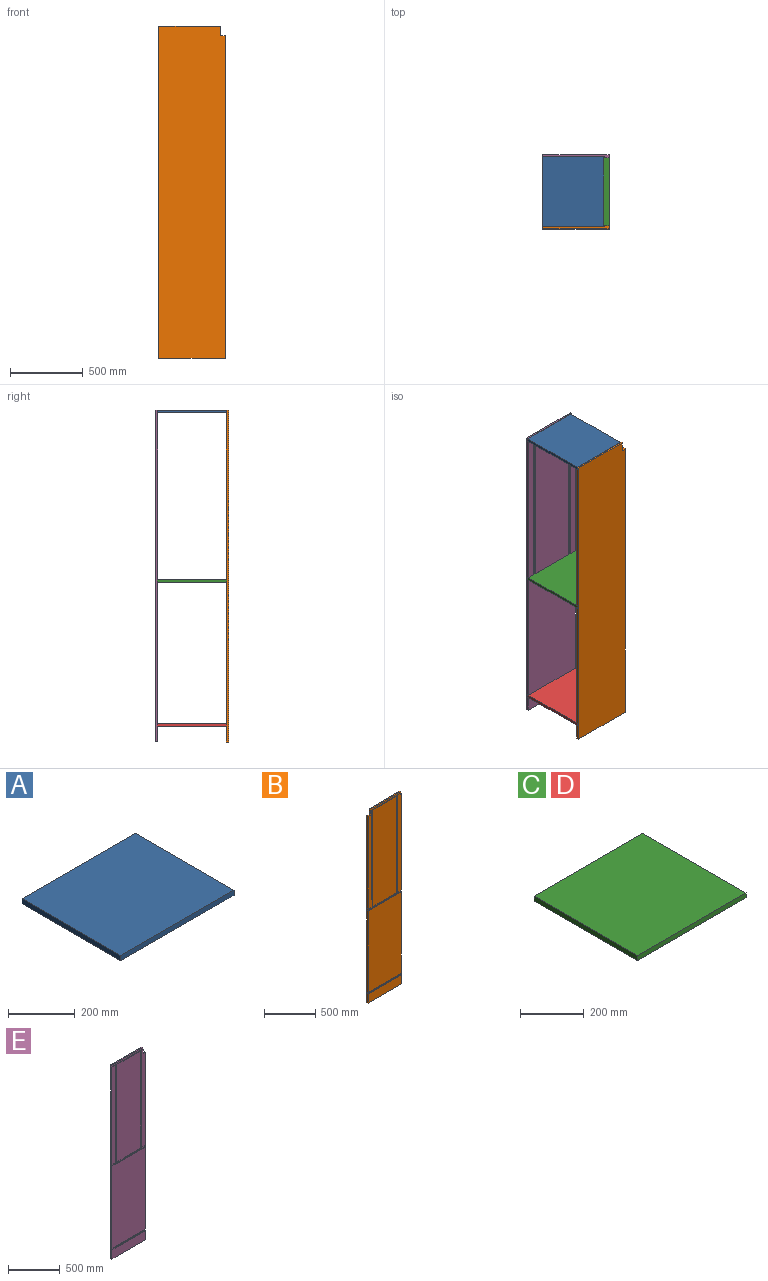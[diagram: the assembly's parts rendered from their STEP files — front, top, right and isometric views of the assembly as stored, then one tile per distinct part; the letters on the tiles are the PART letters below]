
ASSEMBLY  parts=5 mates=12
PART A: 6 faces, bbox 481.3x419.1x19.1 mm
  f0: plane 419.1x19.05mm, normal (-1,0,0), area 7983.9mm2, adj f1,f3,f4,f5
  f1: plane 481.33x19.05mm, normal (0,-1,0), area 9169.3mm2, adj f0,f2,f4,f5
  f2: plane 419.1x19.05mm, normal (1,0,0), area 7983.9mm2, adj f1,f3,f4,f5
  f3: plane 481.33x19.05mm, normal (0,1,0), area 9169.3mm2, adj f0,f2,f4,f5
  f4: plane 481.33x419.1mm, normal (0,0,1), area 201725.4mm2, adj f0,f1,f2,f3
  f5: plane 481.33x419.1mm, normal (0,0,-1), area 201725.4mm2, adj f0,f1,f2,f3
PART B: 26 faces, bbox 457.2x19.1x2286 mm
  f0: plane 1149.1x50.8mm, normal (0,-1,0), area 56878.3mm2, adj f2,f3,f9,f12,f13,f23
  f1: plane 1149.1x323.85mm, normal (0,-1,0), area 372134.7mm2, adj f2,f3,f21,f24
  f2: plane 425.2x6.35mm, normal (0,0,1), area 2548.8mm2, adj f0,f1,f6,f11,f13,f14,f20,f21
  f3: plane 457.2x6.35mm, normal (0,0,-1), area 2752mm2, adj f0,f1,f6,f9,f11,f16,f20,f21
  f4: plane 425.2x12.7mm, normal (0,0,1), area 5400mm2, adj f8,f11,f13,f14
  f5: plane 971.3x457.2mm, normal (0,-1,0), area 444076.5mm2, adj f9,f11,f15,f18
  f6: plane 1149.1x50.8mm, normal (0,-1,0), area 58374.1mm2, adj f2,f3,f11,f20
  f7: plane 457.2x107.7mm, normal (0,-1,0), area 49238.6mm2, adj f9,f10,f11,f17
  f8: plane 2286x457.2mm, normal (0,1,0), area 1043045.7mm2, adj f4,f9,f10,f11,f12,f13
  f9: plane 2219.96x19.05mm, normal (-1,0,0), area 42045.1mm2, adj f0,f3,f5,f7,f8,f10,f12,f15
  f10: plane 457.2x19.05mm, normal (0,0,-1), area 8709.7mm2, adj f7,f8,f9,f11
  f11: plane 2286x19.05mm, normal (1,0,0), area 43180.6mm2, adj f2,f3,f4,f5,f6,f7,f8,f10
  f12: plane 32x19.05mm, normal (0,0,1), area 609.7mm2, adj f0,f8,f9,f13
  f13: plane 66.04x19.05mm, normal (-1,0,0), area 1135.5mm2, adj f0,f2,f4,f8,f12,f14
  f14: plane 425.2x19.3mm, normal (0,-1,0), area 8208mm2, adj f2,f4,f11,f13
  f15: plane 457.2x6.35mm, normal (0,0,1), area 2903.2mm2, adj f5,f9,f11,f16
  f16: plane 457.2x19.3mm, normal (0,-1,0), area 8825.8mm2, adj f3,f9,f11,f15
  f17: plane 457.2x6.35mm, normal (0,0,1), area 2903.2mm2, adj f7,f9,f11,f19
  f18: plane 457.2x6.35mm, normal (0,0,-1), area 2903.2mm2, adj f5,f9,f11,f19
  f19: plane 457.2x19.3mm, normal (0,-1,0), area 8825.8mm2, adj f9,f11,f17,f18
  f20: plane 1149.1x4.76mm, normal (-1,0,0), area 5472.6mm2, adj f2,f3,f6,f22
  f21: plane 1149.1x4.76mm, normal (1,0,0), area 5472.6mm2, adj f1,f2,f3,f22
  f22: plane 1149.1x15.88mm, normal (0,-1,0), area 18241.9mm2, adj f2,f3,f20,f21
  f23: plane 1149.1x4.76mm, normal (1,0,0), area 5472.6mm2, adj f0,f2,f3,f25
  f24: plane 1149.1x4.76mm, normal (-1,0,0), area 5472.6mm2, adj f1,f2,f3,f25
  f25: plane 1149.1x15.88mm, normal (0,-1,0), area 18241.9mm2, adj f2,f3,f23,f24
PART C: 6 faces, bbox 481.3x457.2x19.1 mm
  f0: plane 457.2x19.05mm, normal (-1,0,0), area 8709.7mm2, adj f1,f3,f4,f5
  f1: plane 481.33x19.05mm, normal (0,-1,0), area 9169.3mm2, adj f0,f2,f4,f5
  f2: plane 457.2x19.05mm, normal (1,0,0), area 8709.7mm2, adj f1,f3,f4,f5
  f3: plane 481.33x19.05mm, normal (0,1,0), area 9169.3mm2, adj f0,f2,f4,f5
  f4: plane 481.33x457.2mm, normal (0,0,1), area 220064.1mm2, adj f0,f1,f2,f3
  f5: plane 481.33x457.2mm, normal (0,0,-1), area 220064.1mm2, adj f0,f1,f2,f3
PART D: same geometry as C
PART E: 26 faces, bbox 457.2x19.1x2286 mm
  f0: plane 1149.1x50.8mm, normal (0,-1,0), area 58374.1mm2, adj f2,f3,f7,f23
  f1: plane 1149.1x323.85mm, normal (0,-1,0), area 372134.7mm2, adj f2,f3,f21,f24
  f2: plane 425.2x6.35mm, normal (0,0,1), area 2548.8mm2, adj f0,f1,f6,f7,f12,f14,f20,f21
  f3: plane 457.2x6.35mm, normal (0,0,-1), area 2752mm2, adj f0,f1,f6,f7,f9,f16,f20,f21
  f4: plane 425.2x12.7mm, normal (0,0,1), area 5400mm2, adj f7,f11,f12,f14
  f5: plane 971.3x457.2mm, normal (0,-1,0), area 444076.5mm2, adj f7,f9,f15,f18
  f6: plane 1149.1x50.8mm, normal (0,-1,0), area 56878.3mm2, adj f2,f3,f9,f12,f13,f20
  f7: plane 2286x19.05mm, normal (-1,0,0), area 43180.6mm2, adj f0,f2,f3,f4,f5,f8,f10,f11
  f8: plane 457.2x19.05mm, normal (0,0,-1), area 8709.7mm2, adj f7,f9,f10,f11
  f9: plane 2219.96x19.05mm, normal (1,0,0), area 42045.1mm2, adj f3,f5,f6,f8,f10,f11,f13,f15
  f10: plane 457.2x107.7mm, normal (0,-1,0), area 49238.6mm2, adj f7,f8,f9,f17
  f11: plane 2286x457.2mm, normal (0,1,0), area 1043045.7mm2, adj f4,f7,f8,f9,f12,f13
  f12: plane 66.04x19.05mm, normal (1,0,0), area 1135.5mm2, adj f2,f4,f6,f11,f13,f14
  f13: plane 32x19.05mm, normal (0,0,1), area 609.7mm2, adj f6,f9,f11,f12
  f14: plane 425.2x19.3mm, normal (0,-1,0), area 8208mm2, adj f2,f4,f7,f12
  f15: plane 457.2x6.35mm, normal (0,0,1), area 2903.2mm2, adj f5,f7,f9,f16
  f16: plane 457.2x19.3mm, normal (0,-1,0), area 8825.8mm2, adj f3,f7,f9,f15
  f17: plane 457.2x6.35mm, normal (0,0,1), area 2903.2mm2, adj f7,f9,f10,f19
  f18: plane 457.2x6.35mm, normal (0,0,-1), area 2903.2mm2, adj f5,f7,f9,f19
  f19: plane 457.2x19.3mm, normal (0,-1,0), area 8825.8mm2, adj f7,f9,f17,f18
  f20: plane 1149.1x4.76mm, normal (-1,0,0), area 5472.6mm2, adj f2,f3,f6,f22
  f21: plane 1149.1x4.76mm, normal (1,0,0), area 5472.6mm2, adj f1,f2,f3,f22
  f22: plane 1149.1x15.88mm, normal (0,-1,0), area 18241.9mm2, adj f2,f3,f20,f21
  f23: plane 1149.1x4.76mm, normal (1,0,0), area 5472.6mm2, adj f0,f2,f3,f25
  f24: plane 1149.1x4.76mm, normal (-1,0,0), area 5472.6mm2, adj f1,f2,f3,f25
  f25: plane 1149.1x15.88mm, normal (0,-1,0), area 18241.9mm2, adj f2,f3,f23,f24
PLACE A rot(axis=(0,0,1),90deg) t=(239.54,-991.24,3260.87)mm
PLACE B rot(axis=(0,0,1),180deg) t=(277.64,-1003.94,994.17)mm
PLACE C rot(axis=(0,0,-1),90deg) t=(-179.56,-509.91,2092.47)mm
PLACE D rot(axis=(0,0,1),90deg) t=(277.64,-991.24,1101.87)mm
PLACE E rot(axis=(-1,0,0),0deg) t=(-179.56,-497.21,994.17)mm
MATE planar E.f19 <-> D.f2  axis (0,-1,0) through (-179.56,-509.91,1121.17)mm
MATE planar A.f5 <-> B.f2  axis (0,0,-1) through (29.99,-750.58,3260.87)mm
MATE planar D.f5 <-> B.f17  axis (0,0,-1) through (49.04,-750.58,1101.87)mm
MATE planar D.f0 <-> B.f19  axis (0,-1,0) through (49.04,-991.24,1111.39)mm
MATE planar B.f4 <-> E.f4  axis (0,0,1) through (33.03,-997.59,3280.17)mm
MATE planar A.f3 <-> E.f7  axis (-1,0,0) through (-179.56,-750.58,3270.39)mm
MATE planar B.f9 <-> C.f3  axis (1,0,0) through (277.64,-994.45,2107.05)mm
MATE planar C.f2 <-> B.f16  axis (0,-1,0) through (49.04,-991.24,2101.99)mm
MATE planar C.f5 <-> E.f15  axis (0,0,-1) through (49.04,-750.58,2092.47)mm
MATE planar A.f0 <-> B.f14  axis (0,-1,0) through (-179.56,-991.24,3279.92)mm
MATE planar D.f3 <-> B.f11  axis (-1,0,0) through (-179.56,-750.58,1111.39)mm
MATE planar B.f11 <-> E.f7  axis (-1,0,0) through (-179.56,-994.47,2136.97)mm
